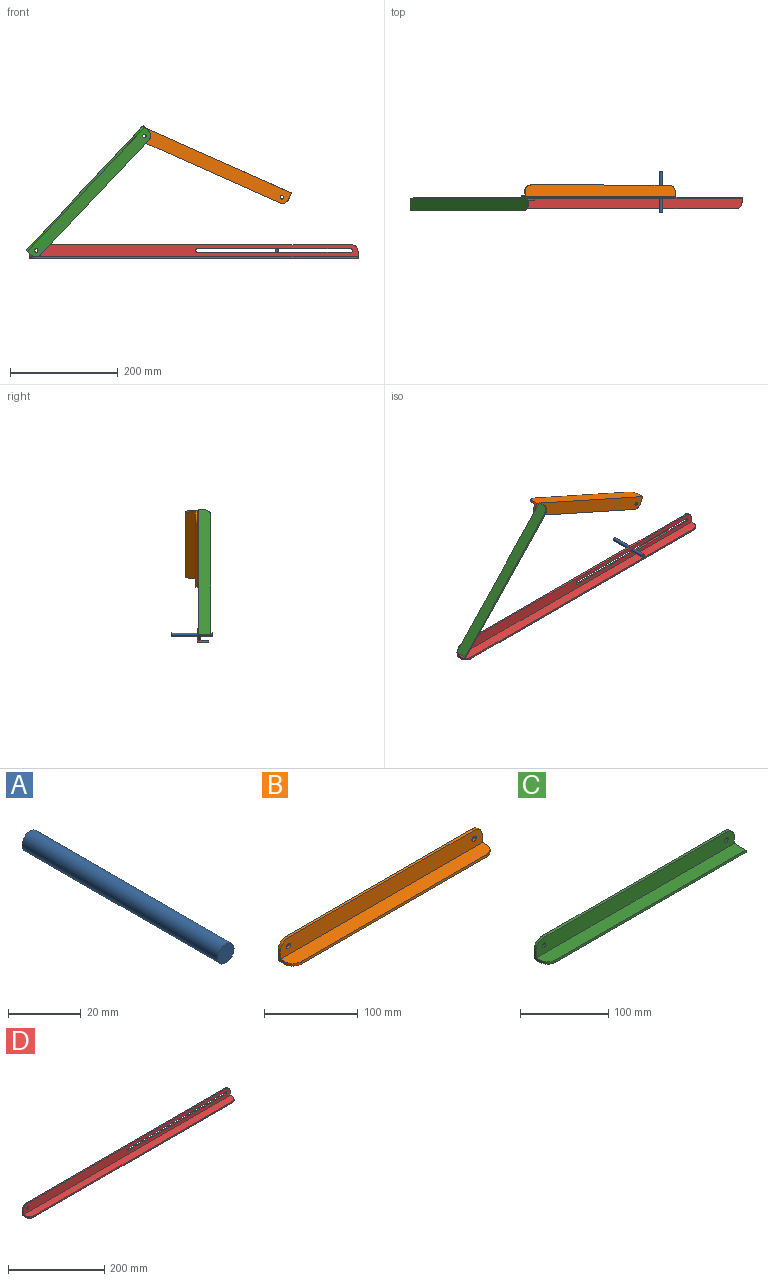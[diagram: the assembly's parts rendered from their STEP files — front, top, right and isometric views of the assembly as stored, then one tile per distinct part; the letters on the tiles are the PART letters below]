
ASSEMBLY  parts=4 mates=3
PART A: 3 faces, bbox 6.4x76.2x6.4 mm
  f0: cylinder r=3.17mm len=76.2mm, axis (0,1,0), area 1520.1mm2, adj f1,f2
  f1: plane 6.35x6.35mm, normal (0,-1,0), area 31.7mm2, adj f0
  f2: plane 6.35x6.35mm, normal (0,1,0), area 31.7mm2, adj f0
PART B: 14 faces, bbox 304.8x22.1x25.4 mm
  f0: plane 279.4x3.3mm, normal (0,0,1), area 922.6mm2, adj f6,f7,f12,f13
  f1: plane 12.7x9.4mm, normal (-1,0,0), area 62.1mm2, adj f2,f6,f7,f8,f10,f12
  f2: plane 304.8x22.1mm, normal (0,0,-1), area 6666.2mm2, adj f1,f4,f7,f9,f10,f11
  f3: cylinder r=3.17mm len=6.35mm, axis (0,1,0), area 65.9mm2, adj f6,f7
  f4: plane 12.7x9.4mm, normal (1,0,0), area 62.1mm2, adj f2,f6,f7,f8,f11,f13
  f5: cylinder r=3.17mm len=6.35mm, axis (0,1,0), area 65.9mm2, adj f6,f7
  f6: plane 304.8x22.1mm, normal (0,-1,0), area 6602.9mm2, adj f0,f1,f3,f4,f5,f8,f12,f13
  f7: plane 304.8x25.4mm, normal (0,1,0), area 7609.4mm2, adj f0,f1,f2,f3,f4,f5,f12,f13
  f8: plane 304.8x18.8mm, normal (0,0,1), area 5659.8mm2, adj f1,f4,f6,f9,f10,f11
  f9: plane 279.4x3.3mm, normal (0,-1,0), area 922.6mm2, adj f2,f8,f10,f11
  f10: cylinder r=12.7mm len=12.7mm, axis (0,0,1), area 65.9mm2, adj f1,f2,f8,f9
  f11: cylinder r=12.7mm len=12.7mm, axis (0,0,-1), area 65.9mm2, adj f2,f4,f8,f9
  f12: cylinder r=12.7mm len=12.7mm, axis (0,-1,0), area 65.9mm2, adj f0,f1,f6,f7
  f13: cylinder r=12.7mm len=12.7mm, axis (0,1,0), area 65.9mm2, adj f0,f4,f6,f7
PART C: 13 faces, bbox 317.5x22.1x25.4 mm
  f0: plane 292.1x3.3mm, normal (0,0,1), area 964.5mm2, adj f6,f7,f11,f12
  f1: plane 12.7x9.4mm, normal (-1,0,0), area 62.1mm2, adj f2,f6,f7,f8,f10,f11
  f2: plane 317.5x22.1mm, normal (0,0,-1), area 6981.5mm2, adj f1,f4,f7,f9,f10
  f3: cylinder r=3.17mm len=6.35mm, axis (0,1,0), area 65.9mm2, adj f6,f7
  f4: plane 22.1x12.7mm, normal (1,0,0), area 104mm2, adj f2,f6,f7,f8,f9,f12
  f5: cylinder r=3.17mm len=6.35mm, axis (0,1,0), area 65.9mm2, adj f6,f7
  f6: plane 317.5x22.1mm, normal (0,-1,0), area 6883.6mm2, adj f0,f1,f3,f4,f5,f8,f11,f12
  f7: plane 317.5x25.4mm, normal (0,1,0), area 7931.9mm2, adj f0,f1,f2,f3,f4,f5,f11,f12
  f8: plane 317.5x18.8mm, normal (0,0,1), area 5933.1mm2, adj f1,f4,f6,f9,f10
  f9: plane 304.8x3.3mm, normal (0,-1,0), area 1006.4mm2, adj f2,f4,f8,f10
  f10: cylinder r=12.7mm len=12.7mm, axis (0,0,1), area 65.9mm2, adj f1,f2,f8,f9
  f11: cylinder r=12.7mm len=12.7mm, axis (0,-1,0), area 65.9mm2, adj f0,f1,f6,f7
  f12: cylinder r=12.7mm len=12.7mm, axis (0,1,0), area 65.9mm2, adj f0,f4,f6,f7
PART D: 17 faces, bbox 609.6x22.1x25.4 mm
  f0: cylinder r=3.17mm len=6.35mm, axis (0,1,0), area 32.9mm2, adj f1,f8,f9,f10
  f1: plane 285.75x3.3mm, normal (0,0,1), area 943.5mm2, adj f0,f2,f9,f10
  f2: cylinder r=3.17mm len=6.35mm, axis (0,1,0), area 32.9mm2, adj f1,f8,f9,f10
  f3: plane 12.7x9.4mm, normal (1,0,0), area 62.1mm2, adj f7,f9,f10,f11,f14,f16
  f4: plane 584.2x3.3mm, normal (0,0,1), area 1929mm2, adj f9,f10,f15,f16
  f5: plane 12.7x9.4mm, normal (-1,0,0), area 62.1mm2, adj f7,f9,f10,f11,f13,f15
  f6: cylinder r=3.17mm len=6.35mm, axis (0,1,0), area 65.9mm2, adj f9,f10
  f7: plane 609.6x22.1mm, normal (0,0,-1), area 13401.7mm2, adj f3,f5,f10,f12,f13,f14
  f8: plane 285.75x3.3mm, normal (0,0,-1), area 943.5mm2, adj f0,f2,f9,f10
  f9: plane 609.6x22.1mm, normal (0,-1,0), area 11523.9mm2, adj f0,f1,f2,f3,f4,f5,f6,f8
  f10: plane 609.6x25.4mm, normal (0,1,0), area 13536.8mm2, adj f0,f1,f2,f3,f4,f5,f6,f7
  f11: plane 609.6x18.8mm, normal (0,0,1), area 11388.8mm2, adj f3,f5,f9,f12,f13,f14
  f12: plane 584.2x3.3mm, normal (0,-1,0), area 1929mm2, adj f7,f11,f13,f14
  f13: cylinder r=12.7mm len=12.7mm, axis (0,0,1), area 65.9mm2, adj f5,f7,f11,f12
  f14: cylinder r=12.7mm len=12.7mm, axis (0,0,-1), area 65.9mm2, adj f3,f7,f11,f12
  f15: cylinder r=12.7mm len=12.7mm, axis (0,-1,0), area 65.9mm2, adj f4,f5,f9,f10
  f16: cylinder r=12.7mm len=12.7mm, axis (0,1,0), area 65.9mm2, adj f3,f4,f9,f10
PLACE A t=(151.94,58.55,2.17)mm
PLACE B rot(axis=(0.98,0,-0.21),180deg) t=(192.5,11.05,136.84)mm
PLACE C rot(axis=(0,1,0),133.3deg) t=(-195.14,7.75,109.51)mm
PLACE D t=(-2.08,11.05,0.51)mm fixed
MATE pin_slot A.f0 <-> D.f2  axis (0,-1,0) through (151.94,20.45,2.17)mm
MATE revolute D.f6 <-> C.f5  axis (0,-1,0) through (-294.18,7.75,2.17)mm
MATE revolute C.f3 <-> B.f3  axis (0,1,0) through (-93.69,7.75,214.6)mm
